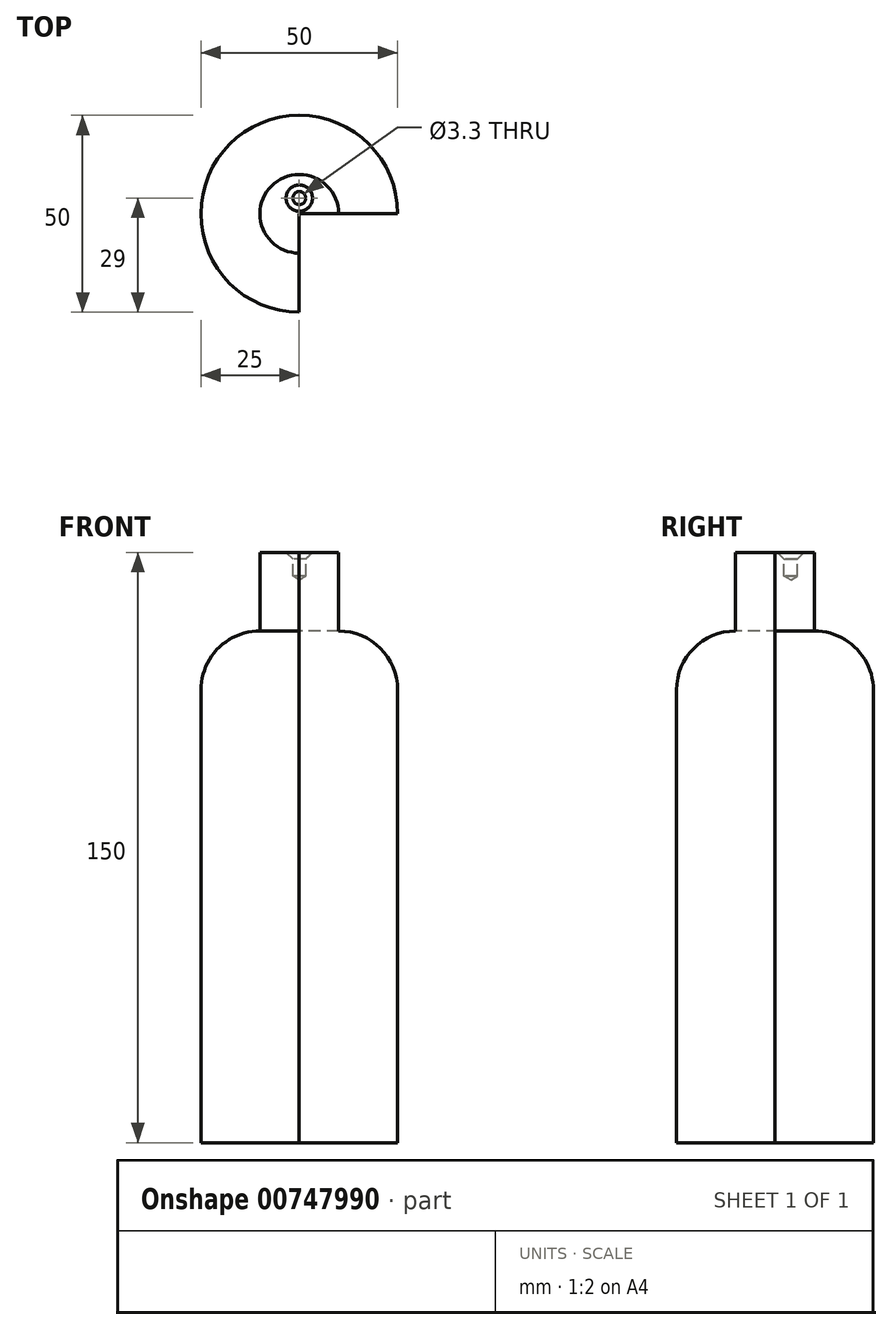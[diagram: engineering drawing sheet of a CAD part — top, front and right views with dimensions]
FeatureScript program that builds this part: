
annotation { "Feature Type Name" : "Feature", "Feature Type Description" : "" }
export const myFeature = defineFeature(function(context is Context, id is Id, definition is map)
    precondition{}
    {
        {
            var Q0;
            Q0=qCreatedBy(makeId("Top.planeOp"),FACE);
            var sketch = newSketch(context, id + "F0", { "sketchPlane" : qUnion([Q0])});
            skCircle(sketch, "E0", {"center": v(0, 0) * mm, "radius": 25 * mm});
            skCircle(sketch, "E1", {"center": v(0, 0) * mm, "radius": 10 * mm});
            skSolve(sketch);
        }
        {
            var Q0;
            Q0=makeQuery(id+"F0.imprint","IMPRINT",FACE,{"disambiguationData":[TD([[makeQuery(id+"F0.imprint","IMPRINT",EDGE,{"derivedFrom":sQuery(id+"F0.wireOp",EDGE,"E0")}),1.0]])]});
            var Q1;
            Q1=makeQuery(id+"F0.imprint","IMPRINT",FACE,{"disambiguationData":[TD([[makeQuery(id+"F0.imprint","IMPRINT",EDGE,{"derivedFrom":sQuery(id+"F0.wireOp",EDGE,"E1")}),1.0]])]});
            extrude(context, id + "F1", {"entities" : qUnion([Q0, Q1]), "oppositeDirection" : true, "depth" : 130 * mm, "offsetDistance" : 25 * mm});
        }
        {
            var Q0;
            Q0=makeQuery(id+"F1.opExtrude","CAP_EDGE",EDGE,{"disambiguationData":[OSD([sQuery(id+"F0.wireOp",EDGE,"E0")])],"isStart":true});
            fillet(context, id + "F2", {"entities" : qUnion([Q0]), "radius" : 15 * mm, "tangentPropagation" : true, "allowEdgeOverflow" : false});
        }
        {
            var Q0;
            Q0=makeQuery(id+"F0.imprint","IMPRINT",FACE,{"disambiguationData":[TD([[makeQuery(id+"F0.imprint","IMPRINT",EDGE,{"derivedFrom":sQuery(id+"F0.wireOp",EDGE,"E1")}),1.0]])]});
            extrude(context, id + "F3", {"entities" : qUnion([Q0]), "operationType" : NewBodyOperationType.ADD, "depth" : 20 * mm, "offsetDistance" : 25 * mm});
        }
        {
            var Q0;
            Q0=qCreatedBy(makeId("Top.planeOp"),FACE);
            var sketch = newSketch(context, id + "F4", { "sketchPlane" : qUnion([Q0])});
            skLineSegment(sketch, "E2.bottom", {"start": v(0, 0) * mm, "end": v(74.85, 0) * mm});
            skLineSegment(sketch, "E2.top", {"start": v(0, -49.52) * mm, "end": v(74.85, -49.52) * mm});
            skLineSegment(sketch, "E2.left", {"start": v(0, 0) * mm, "end": v(0, -49.52) * mm});
            skLineSegment(sketch, "E2.right", {"start": v(74.85, 0) * mm, "end": v(74.85, -49.52) * mm});
            skSolve(sketch);
        }
        {
            var Q0;
            Q0=makeQuery(id+"F4.imprint","IMPRINT",FACE,{"disambiguationData":[TD([[makeQuery(id+"F4.imprint","IMPRINT",EDGE,{"derivedFrom":sQuery(id+"F4.wireOp",EDGE,"E2.bottom")}),-1.0]])]});
            extrude(context, id + "F5", {"entities" : qUnion([Q0]), "operationType" : NewBodyOperationType.REMOVE, "endBound" : BoundingType.THROUGH_ALL, "depth" : 25 * mm, "offsetDistance" : 25 * mm, "hasSecondDirection" : true, "secondDirectionBound" : SecondDirectionBoundingType.THROUGH_ALL, "secondDirectionOppositeDirection" : true, "secondDirectionDepth" : 25 * mm});
        }
        {
            var Q0;
            Q0=makeQuery(id+"F3.opExtrude","CAP_FACE",FACE,{"disambiguationData":[OSD([sQuery(id+"F0.wireOp",EDGE,"E1")])],"isStart":false});
            var sketch = newSketch(context, id + "F6", { "sketchPlane" : qUnion([Q0])});
            skPoint(sketch, "E3", {"position": v(0, 4) * mm});
            skSolve(sketch);
        }
        {
            var Q0;
            Q0=sQuery(id+"F6.wireOp",VERTEX,"E3");
            var Q1;
            Q1=makeQuery(id+"F1.opExtrude","SWEPT_BODY",BODY,{"disambiguationData":[OSD([sQuery(id+"F0.wireOp",EDGE,"E0")])]});
            hole(context, id + "F7", {"style" : HoleStyle.C_SINK, "endStyle" : HoleEndStyle.BLIND, "standardTappedOrClearance" : lookupTablePath({ "standard" : "ISO", "fit" : "Normal", "size" : "M3", "type" : "Clearance" }), "standardBlindInLast" : lookupTablePath({ "fit" : "Standard", "standard" : "ISO", "size" : "M3", "type" : "Clearance" }), "holeDiameter" : 3.3 * mm, "cSinkDiameter" : 6.72 * mm, "cSinkAngle" : 90 * degree, "majorDiameter" : 5 * mm, "holeDepth" : 6 * mm, "isTappedThrough" : true, "tappedDepth" : 12 * mm, "tapClearance" : 3, "locations" : qUnion([Q0]), "scope" : qUnion([Q1])});
        }
    });
